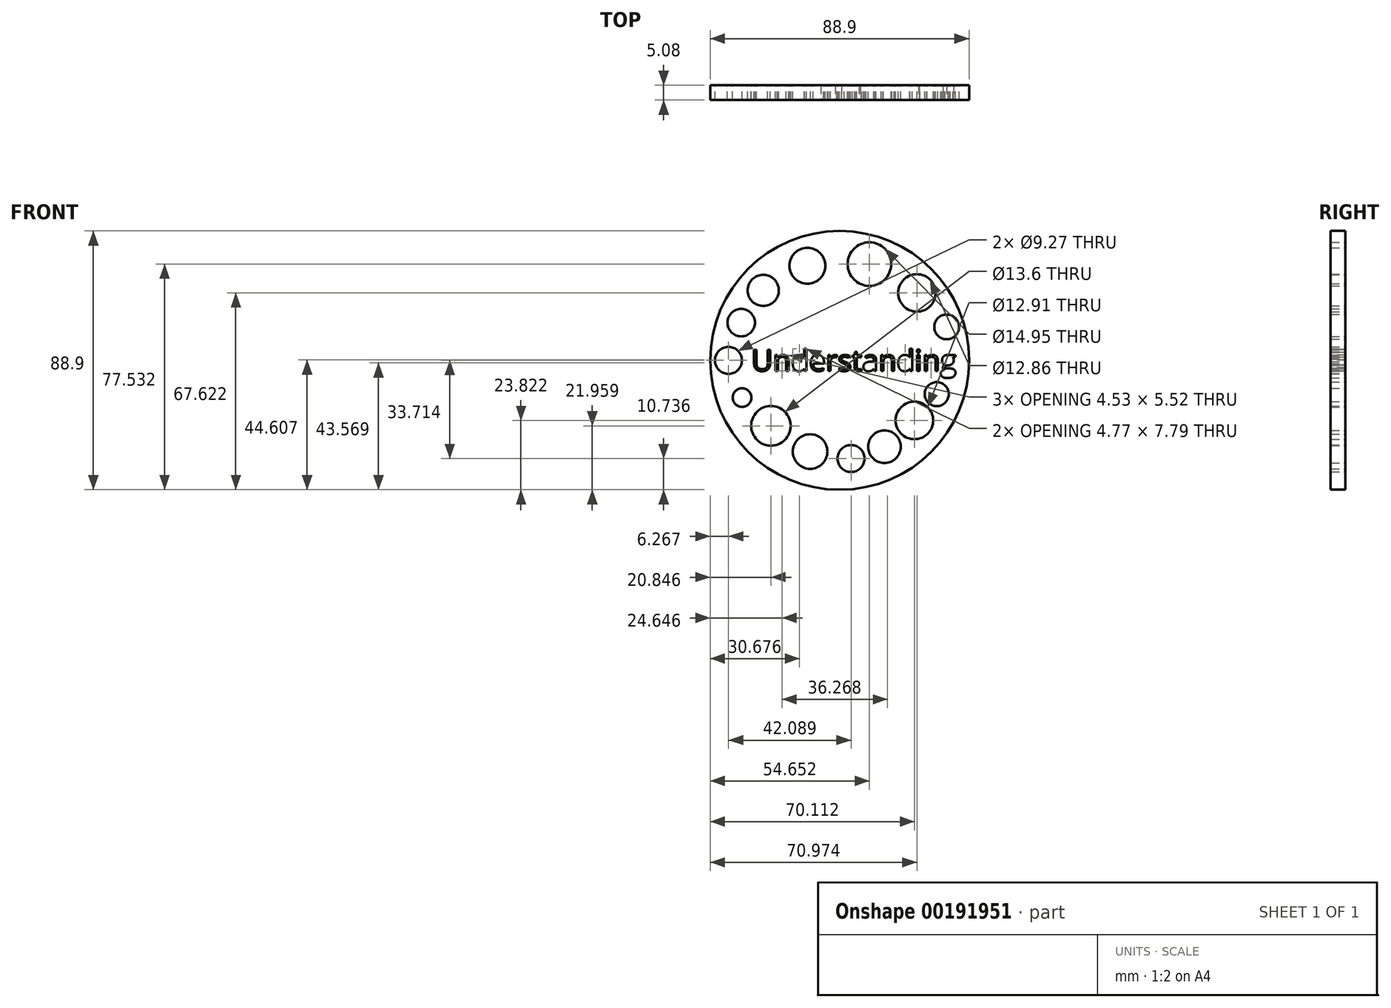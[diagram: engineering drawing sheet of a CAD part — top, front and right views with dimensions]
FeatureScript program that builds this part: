
annotation { "Feature Type Name" : "Feature", "Feature Type Description" : "" }
export const myFeature = defineFeature(function(context is Context, id is Id, definition is map)
    precondition{}
    {
        {
            var Q0;
            Q0=qCreatedBy(makeId("Front.planeOp"),FACE);
            var sketch = newSketch(context, id + "F0", { "sketchPlane" : qUnion([Q0])});
            skCircle(sketch, "E0", {"center": v(0, 0) * mm, "radius": 44.45 * mm});
            skText(sketch, "E1", { "text": "Understanding ", "fontName": "OpenSans-Regular.ttf"});
            skCircle(sketch, "E2", {"center": v(36.73, 11.51) * mm, "radius": 4.25 * mm});
            skCircle(sketch, "E3", {"center": v(26.52, 23.17) * mm, "radius": 6.43 * mm});
            skCircle(sketch, "E4", {"center": v(10.2, 33.08) * mm, "radius": 7.48 * mm});
            skCircle(sketch, "E5", {"center": v(33.33, -11.59) * mm, "radius": 4.14 * mm});
            skCircle(sketch, "E6", {"center": v(25.66, -20.63) * mm, "radius": 6.46 * mm});
            skCircle(sketch, "E7", {"center": v(-38.18, 0) * mm, "radius": 4.63 * mm});
            skCircle(sketch, "E8", {"center": v(-33.81, 12.97) * mm, "radius": 4.73 * mm});
            skCircle(sketch, "E9", {"center": v(-26.23, 24.05) * mm, "radius": 5.35 * mm});
            skCircle(sketch, "E10", {"center": v(-11.08, 32.5) * mm, "radius": 6.16 * mm});
            skCircle(sketch, "E11", {"center": v(15.36, -29.66) * mm, "radius": 5.6 * mm});
            skCircle(sketch, "E12", {"center": v(3.9, -33.71) * mm, "radius": 4.63 * mm});
            skCircle(sketch, "E13", {"center": v(-10.16, -31.32) * mm, "radius": 5.93 * mm});
            skCircle(sketch, "E14", {"center": v(-23.6, -22.5) * mm, "radius": 6.8 * mm});
            skCircle(sketch, "E15", {"center": v(-33.53, -12.8) * mm, "radius": 3.22 * mm});
            const initialGuessF0  = {"E1": [-0.03031, -0.00364, 1, 0, 0.00729]};
            skSetInitialGuess(sketch, initialGuessF0);
            skSolve(sketch);
        }
        {
            var Q0;
            Q0 = qSketchRegion(id + "F0", true);
            extrude(context, id + "F1", {"entities" : qUnion([Q0]), "depth" : 5.08 * mm});
        }
    });
